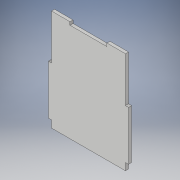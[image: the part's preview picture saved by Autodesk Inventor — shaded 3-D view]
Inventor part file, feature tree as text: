
AUTODESK INVENTOR PART (.ipt)
format: ipt  version: 2019 (Build 230136000, 136)  size: 124,928 bytes
history: native  units: in
note: dims shown in document units (in); Inventor stores cm internally (conversion verified against a paired STEP export)
features: extrude x3, sketch x3
ambient origin geometry x8: Origin, YZ Plane, XZ Plane, XY Plane, X Axis, Y Axis, Z Axis, Center Point
bodies: Solid1 (feature_tree)
feature tree (6):
  extrude  "Extrusion1"  Depth=3.111in
  extrude  "Extrusion2"  Depth=2.0in
  extrude  "Extrusion3"  Depth=0.125in
  sketch  "Sketch1"  dims[d0=3.0in d1=3.111in]
  sketch  "Sketch2"  dims[d2=0.289in d3=2.0in]
  sketch  "Sketch3"  dims[d4=0.125in d5=0.0in d6=0.125in d7=1.0in d8=0.125in d9=0.0in d10=0.125in d11=1.5in d12=0.75in d13=0.125in d14=0.0in]
